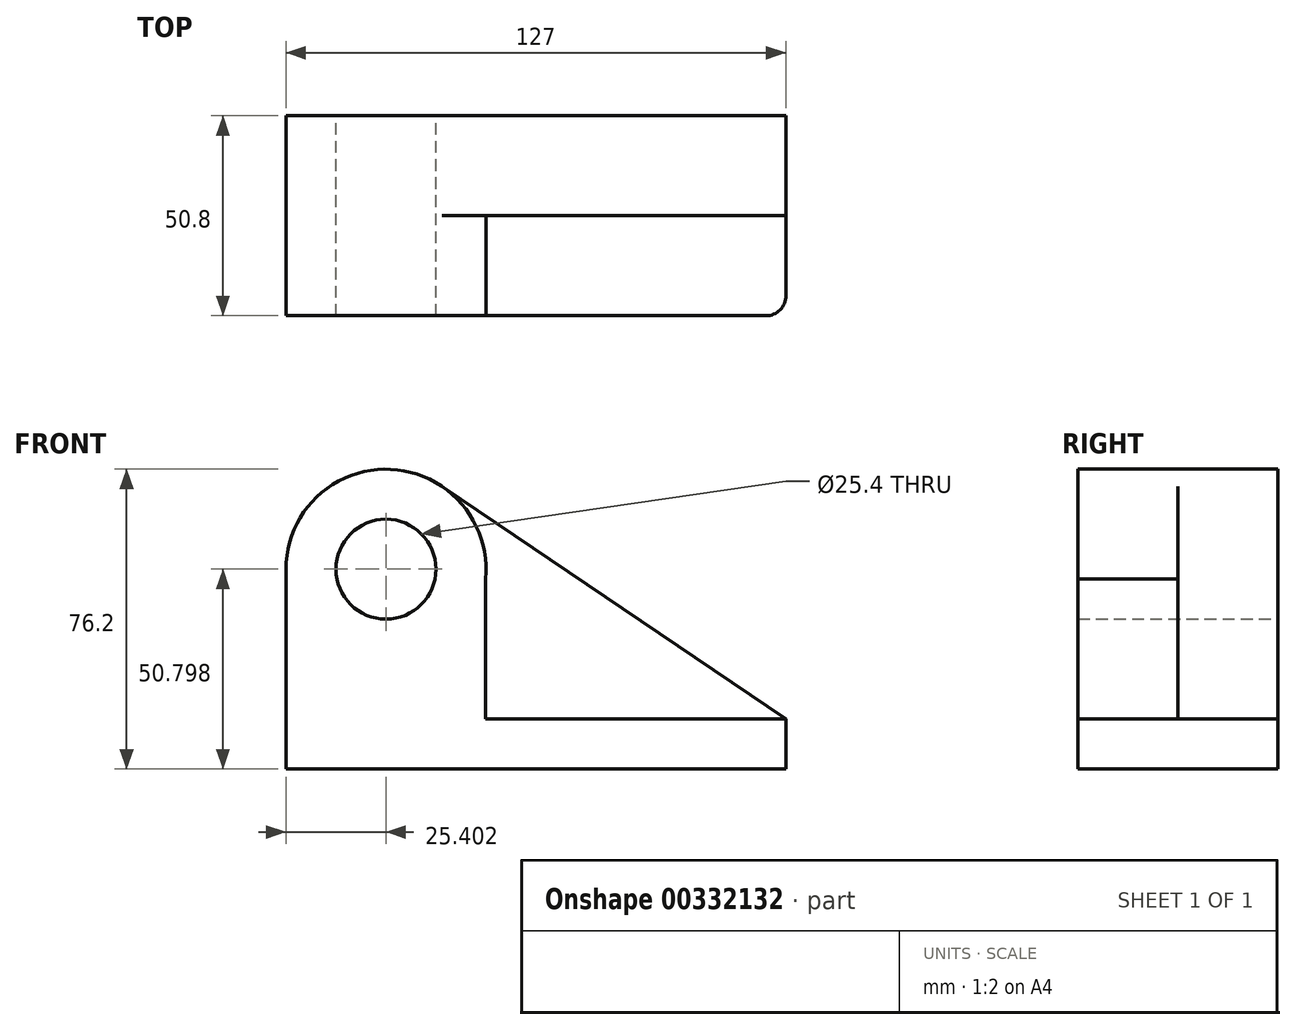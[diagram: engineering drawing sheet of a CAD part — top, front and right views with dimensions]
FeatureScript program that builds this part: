
annotation { "Feature Type Name" : "Feature", "Feature Type Description" : "" }
export const myFeature = defineFeature(function(context is Context, id is Id, definition is map)
    precondition{}
    {
        {
            var Q0;
            Q0=qCreatedBy(makeId("Front.planeOp"),FACE);
            var sketch = newSketch(context, id + "F0", { "sketchPlane" : qUnion([Q0])});
            skCircle(sketch, "E0", {"center": v(-26.52, 19.56) * mm, "radius": 12.7 * mm});
            skArc(sketch, "E1", {"start": v(-12.28, 40.6) * mm, "mid": v(-38.42, 42) * mm, "end": v(-51.92, 19.56) * mm});
            skLineSegment(sketch, "E2", {"start": v(-51.92, 19.56) * mm, "end": v(-51.92, -31.24) * mm});
            skLineSegment(sketch, "E3", {"start": v(-51.92, -31.24) * mm, "end": v(75.08, -31.24) * mm});
            skLineSegment(sketch, "E4", {"start": v(75.08, -31.24) * mm, "end": v(75.08, -18.54) * mm});
            skLineSegment(sketch, "E5", {"start": v(75.08, -18.54) * mm, "end": v(-12.28, 40.6) * mm});
            skSolve(sketch);
        }
        {
            var Q0;
            Q0=makeQuery(id+"F0.imprint","IMPRINT",FACE,{"disambiguationData":[TD([[makeQuery(id+"F0.imprint","IMPRINT",EDGE,{"derivedFrom":sQuery(id+"F0.wireOp",EDGE,"E0")}),-1.0]])]});
            extrude(context, id + "F1", {"entities" : qUnion([Q0]), "depth" : 25.4 * mm});
        }
        {
            var Q0;
            Q0=makeQuery(id+"F1.opExtrude","CAP_FACE",FACE,{"disambiguationData":[OSD([sQuery(id+"F0.wireOp",EDGE,"E0"),sQuery(id+"F0.wireOp",EDGE,"E1"),sQuery(id+"F0.wireOp",EDGE,"E2"),sQuery(id+"F0.wireOp",EDGE,"E3"),sQuery(id+"F0.wireOp",EDGE,"E4"),sQuery(id+"F0.wireOp",EDGE,"E5")])],"isStart":false});
            var sketch = newSketch(context, id + "F2", { "sketchPlane" : qUnion([Q0])});
            skCircle(sketch, "E6", {"center": v(-26.52, 19.56) * mm, "radius": 12.7 * mm});
            skLineSegment(sketch, "E7.bottom", {"start": v(75.08, -18.54) * mm, "end": v(-1.23, -18.54) * mm});
            skLineSegment(sketch, "E7.top", {"start": v(75.08, -31.24) * mm, "end": v(-51.92, -31.24) * mm});
            skLineSegment(sketch, "E7.left", {"start": v(75.08, -18.54) * mm, "end": v(75.08, -31.24) * mm});
            skLineSegment(sketch, "E7.right", {"start": v(-51.92, -18.54) * mm, "end": v(-51.92, -31.24) * mm});
            skLineSegment(sketch, "E8", {"start": v(-1.23, -18.54) * mm, "end": v(-1.23, 17.14) * mm});
            skLineSegment(sketch, "E9", {"start": v(-51.92, 19.56) * mm, "end": v(-51.92, -18.54) * mm});
            skArc(sketch, "E10", {"start": v(-1.23, 17.14) * mm, "mid": v(-25.3, 44.93) * mm, "end": v(-51.92, 19.56) * mm});
            skSolve(sketch);
        }
        {
            var Q0;
            Q0=makeQuery(id+"F2.imprint","IMPRINT",FACE,{"disambiguationData":[TD([[makeQuery(id+"F2.imprint","IMPRINT",EDGE,{"derivedFrom":sQuery(id+"F2.wireOp",EDGE,"E6")}),-1.0]])]});
            extrude(context, id + "F3", {"entities" : qUnion([Q0]), "operationType" : NewBodyOperationType.ADD, "depth" : 25.4 * mm});
        }
        {
            var Q0;
            Q0=makeQuery(id+"F3.opExtrude","CAP_EDGE",EDGE,{"disambiguationData":[OSD([sQuery(id+"F2.wireOp",EDGE,"E7.left")])],"isStart":false});
            fillet(context, id + "F4", {"entities" : qUnion([Q0]), "radius" : 5.08 * mm, "tangentPropagation" : true, "allowEdgeOverflow" : false});
        }
    });
